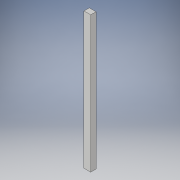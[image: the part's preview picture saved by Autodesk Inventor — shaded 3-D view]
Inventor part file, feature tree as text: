
AUTODESK INVENTOR PART (.ipt)
format: ipt  version: 2019 (Build 230136000, 136)  size: 95,232 bytes
history: native  units: in
note: dims shown in document units (in); Inventor stores cm internally (conversion verified against a paired STEP export)
features: extrude x1, sketch x1
ambient origin geometry x8: Origin, YZ Plane, XZ Plane, XY Plane, X Axis, Y Axis, Z Axis, Center Point
bodies: Solid1 (feature_tree)
feature tree (2):
  extrude  "Extrusion1"  [1 undecoded]
  sketch  "Sketch1"  dims[d0=0.0197in d1=0.0in]
note: 1 required parameter value undecoded (feature->parameter linkage not recoverable at this tier; creation-order binding heuristic only, values carry confidence <= 0.55)
